# Revit family: Stufenwinkel 40-5 3-Lo
name_source: partatom
category: HLS-Bauteile
revit_build: Autodesk Revit 2017 (Build: 20190507_1515(x64)
units: mm (PartAtom-declared; Revit-internal decimal feet)

## family parameters
Arbeitsebenenbasiert = Ja
Beim Laden mit Abzugskörper schneiden = Nein
Bemaßung runder Anschluss = Durchmesser verwenden
Gemeinsam genutzt = Ja
Immer vertikal = Nein
Raumberechnungspunkt = Nein
Teiletyp = Normal

## types (2) — shared parameters
Fabrikat = MEFA
Firma = MEFA Befestigungs- und Montagesysteme GmbH
Kurztext1 = Stufenwinkel 3-Loch C-Profil 45
Material = Stahl
Materialname = S235
Mengeneinheit = St
Oberflaeche = galvanisch verzinkt
Vorgabe-Ansicht = 1219 mm
max. zul. Last = 1.00 kN
vpe = 25 St

## per-type parameters (varying)
| type | Artikelnummer | EAN | Gewicht | Gewicht pro Bauteil | H | Höhe | Kurztext2 |
| Stufenwinkel 45 | 08141245 | 4250928447968 | 0.28 kg | 0.28 kg | 45 mm  [stored 0.147638 ft] | 45 mm | Schienenhöhe 45 mm |
| Stufenwinkel 60 | 08141300 | 4250928419842 | 0.30 kg | 0.30 kg | 60 mm  [stored 0.19685 ft] | 60 mm | Schienenhöhe 60 mm |

note: [stored X ft] marks values corroborated as IEEE doubles in the binary element streams (Revit-internal decimal feet)
